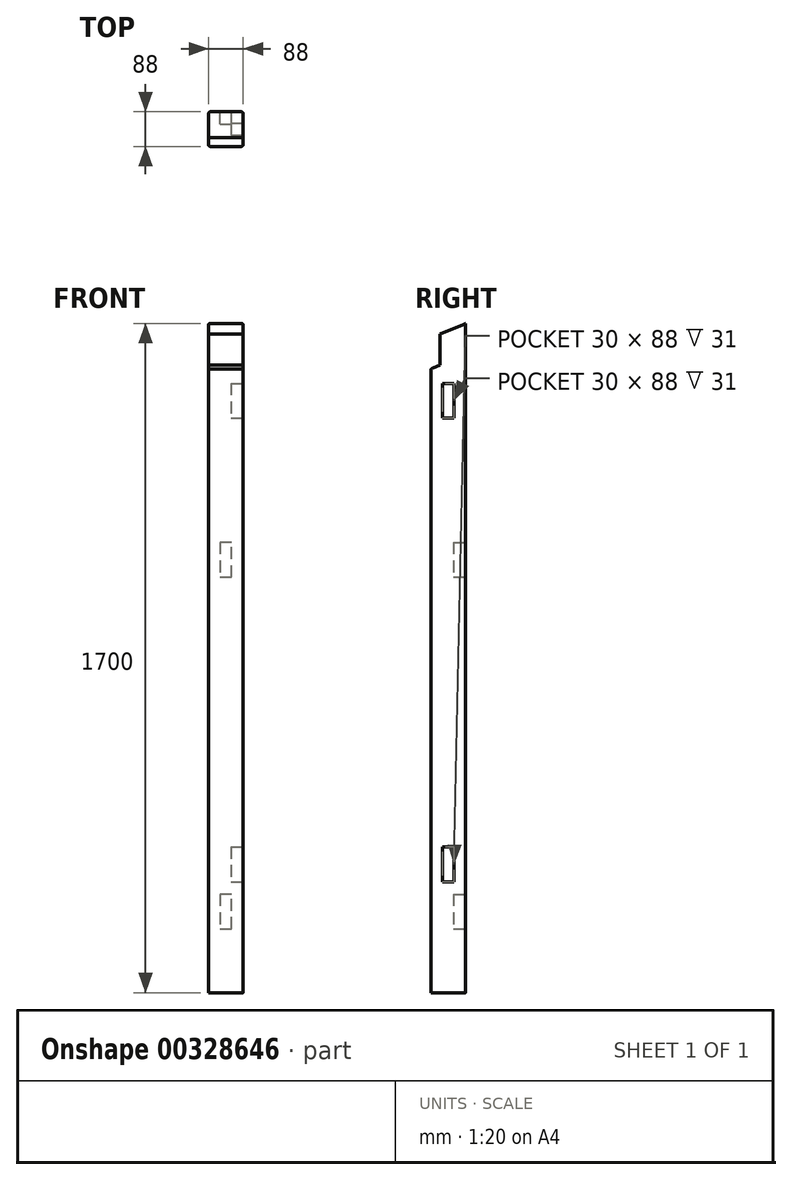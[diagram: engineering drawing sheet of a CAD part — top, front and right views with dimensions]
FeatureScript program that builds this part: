
annotation { "Feature Type Name" : "Feature", "Feature Type Description" : "" }
export const myFeature = defineFeature(function(context is Context, id is Id, definition is map)
    precondition{}
    {
        {
            var Q0;
            Q0=qCreatedBy(makeId("Top.planeOp"),FACE);
            var sketch = newSketch(context, id + "F0", { "sketchPlane" : qUnion([Q0])});
            skLineSegment(sketch, "E0.bottom", {"start": v(0, 0) * mm, "end": v(88, 0) * mm});
            skLineSegment(sketch, "E0.top", {"start": v(0, 88) * mm, "end": v(88, 88) * mm});
            skLineSegment(sketch, "E0.left", {"start": v(0, 0) * mm, "end": v(0, 88) * mm});
            skLineSegment(sketch, "E0.right", {"start": v(88, 0) * mm, "end": v(88, 88) * mm});
            skSolve(sketch);
        }
        {
            var Q0;
            Q0=qSketchRegion(id+"F0",true);
            extrude(context, id + "F1", {"entities" : qUnion([Q0]), "depth" : 1700 * mm});
        }
        {
            var Q0;
            Q0=makeQuery(id+"F1.opExtrude","SWEPT_FACE",FACE,{"disambiguationData":[OSD([sQuery(id+"F0.wireOp",EDGE,"E0.right")])]});
            var sketch = newSketch(context, id + "F2", { "sketchPlane" : qUnion([Q0])});
            skLineSegment(sketch, "E1", {"start": v(44, 0) * mm, "end": v(44, 282) * mm, "construction": true});
            skPoint(sketch, "E1.endSnap0", {"position": v(44, 0) * mm});
            skLineSegment(sketch, "E2", {"start": v(44, 282) * mm, "end": v(29, 282) * mm});
            skLineSegment(sketch, "E3", {"start": v(29, 282) * mm, "end": v(29, 370) * mm});
            skLineSegment(sketch, "E4", {"start": v(29, 370) * mm, "end": v(59, 370) * mm});
            skLineSegment(sketch, "E5", {"start": v(59, 370) * mm, "end": v(59, 282) * mm});
            skLineSegment(sketch, "E6", {"start": v(59, 282) * mm, "end": v(44, 282) * mm});
            skSolve(sketch);
        }
        {
            var Q0;
            Q0=qSketchRegion(id+"F2",true);
            extrude(context, id + "F3", {"entities" : qUnion([Q0]), "operationType" : NewBodyOperationType.REMOVE, "oppositeDirection" : true, "depth" : 31 * mm});
        }
        {
            var Q0;
            Q0=makeQuery(id+"F1.opExtrude","SWEPT_FACE",FACE,{"disambiguationData":[OSD([sQuery(id+"F0.wireOp",EDGE,"E0.right")])]});
            var sketch = newSketch(context, id + "F4", { "sketchPlane" : qUnion([Q0])});
            skLineSegment(sketch, "E7", {"start": v(44, 0) * mm, "end": v(44, 1460) * mm, "construction": true});
            skPoint(sketch, "E7.endSnap0", {"position": v(44, 370) * mm});
            skLineSegment(sketch, "E8", {"start": v(44, 1460) * mm, "end": v(29, 1460) * mm});
            skLineSegment(sketch, "E9", {"start": v(29, 1460) * mm, "end": v(29, 1548) * mm});
            skLineSegment(sketch, "E10", {"start": v(29, 1548) * mm, "end": v(59, 1548) * mm});
            skLineSegment(sketch, "E11", {"start": v(59, 1548) * mm, "end": v(59, 1460) * mm});
            skLineSegment(sketch, "E12", {"start": v(59, 1460) * mm, "end": v(44, 1460) * mm});
            skSolve(sketch);
        }
        {
            var Q0;
            Q0=qSketchRegion(id+"F4",true);
            extrude(context, id + "F5", {"entities" : qUnion([Q0]), "operationType" : NewBodyOperationType.REMOVE, "oppositeDirection" : true, "depth" : 31 * mm});
        }
        {
            var Q0;
            Q0=makeQuery(id+"F1.opExtrude","SWEPT_FACE",FACE,{"disambiguationData":[OSD([sQuery(id+"F0.wireOp",EDGE,"E0.right")])]});
            var sketch = newSketch(context, id + "F6", { "sketchPlane" : qUnion([Q0])});
            skLineSegment(sketch, "E13", {"start": v(88, 1700) * mm, "end": v(0, 1663.55) * mm});
            skLineSegment(sketch, "E14", {"start": v(0, 1663.55) * mm, "end": v(0, 1700) * mm});
            skLineSegment(sketch, "E15", {"start": v(0, 1700) * mm, "end": v(88, 1700) * mm});
            skSolve(sketch);
        }
        {
            var Q0;
            Q0=qSketchRegion(id+"F6",true);
            extrude(context, id + "F7", {"entities" : qUnion([Q0]), "operationType" : NewBodyOperationType.REMOVE, "endBound" : BoundingType.THROUGH_ALL, "oppositeDirection" : true, "depth" : 260.2 * mm});
        }
        {
            var Q0;
            Q0=makeQuery(id+"F1.opExtrude","SWEPT_FACE",FACE,{"disambiguationData":[OSD([sQuery(id+"F0.wireOp",EDGE,"E0.right")])]});
            var sketch = newSketch(context, id + "F8", { "sketchPlane" : qUnion([Q0])});
            skLineSegment(sketch, "E16", {"start": v(23, 1673.08) * mm, "end": v(23, 1594.08) * mm});
            skLineSegment(sketch, "E17", {"start": v(0, 1663.55) * mm, "end": v(23, 1673.08) * mm});
            skLineSegment(sketch, "E18", {"start": v(23, 1594.08) * mm, "end": v(0, 1584.55) * mm});
            skPoint(sketch, "E19.end.orphan", {"position": v(0, 1608.54) * mm});
            skLineSegment(sketch, "E20", {"start": v(0, 1663.55) * mm, "end": v(0, 1584.55) * mm});
            skSolve(sketch);
        }
        {
            var Q0;
            Q0=makeQuery(id+"F8.imprint","IMPRINT",FACE,{"disambiguationData":[TD([[makeQuery(id+"F8.imprint","IMPRINT",EDGE,{"derivedFrom":sQuery(id+"F8.wireOp",EDGE,"E16")}),-1.0]])]});
            extrude(context, id + "F9", {"entities" : qUnion([Q0]), "operationType" : NewBodyOperationType.REMOVE, "endBound" : BoundingType.THROUGH_ALL, "oppositeDirection" : true, "depth" : 204.57 * mm});
        }
        {
            var Q0;
            Q0=makeQuery(id+"F1.opExtrude","SWEPT_FACE",FACE,{"disambiguationData":[OSD([sQuery(id+"F0.wireOp",EDGE,"E0.top")])]});
            var sketch = newSketch(context, id + "F10", { "sketchPlane" : qUnion([Q0])});
            skLineSegment(sketch, "E21", {"start": v(-44, 0) * mm, "end": v(-44, 162) * mm, "construction": true});
            skPoint(sketch, "E21.endSnap0", {"position": v(-44, 0) * mm});
            skLineSegment(sketch, "E22", {"start": v(-44, 162) * mm, "end": v(-59, 162) * mm});
            skLineSegment(sketch, "E23", {"start": v(-59, 162) * mm, "end": v(-59, 250) * mm});
            skLineSegment(sketch, "E24", {"start": v(-59, 250) * mm, "end": v(-29, 250) * mm});
            skLineSegment(sketch, "E25", {"start": v(-29, 250) * mm, "end": v(-29, 162) * mm});
            skLineSegment(sketch, "E26", {"start": v(-29, 162) * mm, "end": v(-44, 162) * mm});
            skSolve(sketch);
        }
        {
            var Q0;
            Q0=qSketchRegion(id+"F10",true);
            extrude(context, id + "F11", {"entities" : qUnion([Q0]), "operationType" : NewBodyOperationType.REMOVE, "oppositeDirection" : true, "depth" : 31 * mm});
        }
        {
            var Q0;
            Q0=makeQuery(id+"F1.opExtrude","SWEPT_FACE",FACE,{"disambiguationData":[OSD([sQuery(id+"F0.wireOp",EDGE,"E0.top")])]});
            var sketch = newSketch(context, id + "F12", { "sketchPlane" : qUnion([Q0])});
            skLineSegment(sketch, "E27", {"start": v(-44, 0) * mm, "end": v(-44, 1056) * mm, "construction": true});
            skLineSegment(sketch, "E28", {"start": v(-44, 1056) * mm, "end": v(-59, 1056) * mm});
            skLineSegment(sketch, "E29", {"start": v(-59, 1056) * mm, "end": v(-59, 1144) * mm});
            skLineSegment(sketch, "E30", {"start": v(-59, 1144) * mm, "end": v(-29, 1144) * mm});
            skLineSegment(sketch, "E31", {"start": v(-29, 1144) * mm, "end": v(-29, 1056) * mm});
            skLineSegment(sketch, "E32", {"start": v(-29, 1056) * mm, "end": v(-44, 1056) * mm});
            skSolve(sketch);
        }
        {
            var Q0;
            Q0=qSketchRegion(id+"F12",true);
            extrude(context, id + "F13", {"entities" : qUnion([Q0]), "operationType" : NewBodyOperationType.REMOVE, "oppositeDirection" : true, "depth" : 31 * mm});
        }
        {
            var Q0;
            Q0=makeQuery(id+"F1.opExtrude","SWEPT_EDGE",EDGE,{"disambiguationData":[OSD([sQuery(id+"F0.wireOp",EDGE,"E0.bottom"),sQuery(id+"F0.wireOp",EDGE,"E0.right")])]});
            var Q1;
            Q1=makeQuery(id+"F1.opExtrude","SWEPT_EDGE",EDGE,{"disambiguationData":[OSD([sQuery(id+"F0.wireOp",EDGE,"E0.bottom"),sQuery(id+"F0.wireOp",EDGE,"E0.left")])]});
            var Q2;
            Q2=makeQuery(id+"F1.opExtrude","SWEPT_EDGE",EDGE,{"disambiguationData":[OSD([sQuery(id+"F0.wireOp",EDGE,"E0.top"),sQuery(id+"F0.wireOp",EDGE,"E0.right")])]});
            var Q3;
            Q3=makeQuery(id+"F1.opExtrude","SWEPT_EDGE",EDGE,{"disambiguationData":[OSD([sQuery(id+"F0.wireOp",EDGE,"E0.top"),sQuery(id+"F0.wireOp",EDGE,"E0.left")])]});
            fillet(context, id + "F14", {"entities" : qUnion([Q0, Q1, Q2, Q3]), "radius" : 5 * mm, "tangentPropagation" : true, "allowEdgeOverflow" : false});
        }
    });
